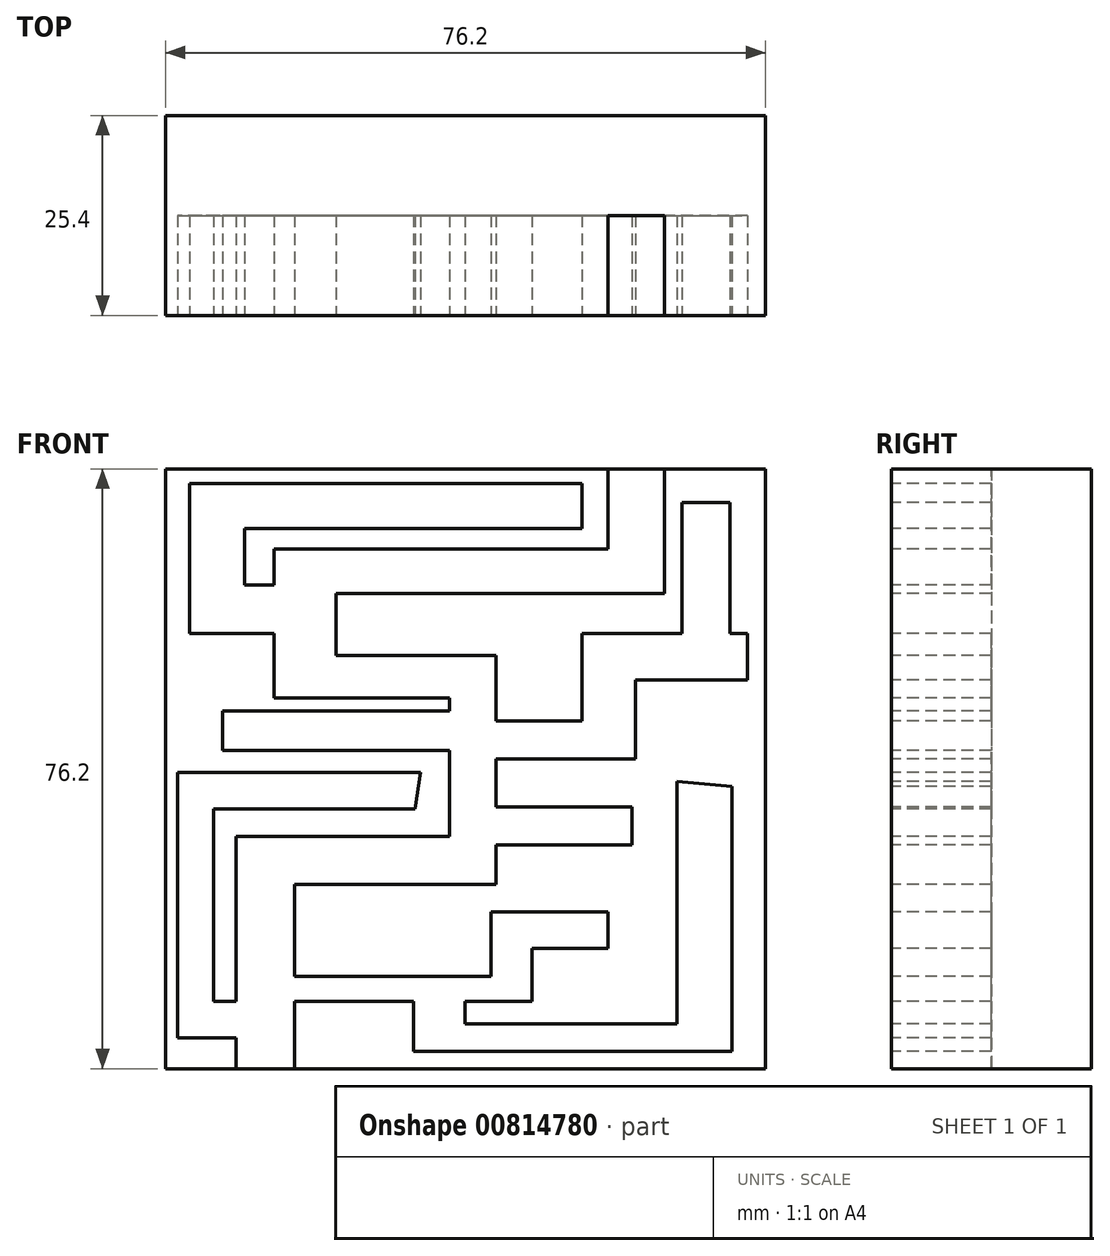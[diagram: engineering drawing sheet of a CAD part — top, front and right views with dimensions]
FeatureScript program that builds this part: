
annotation { "Feature Type Name" : "Feature", "Feature Type Description" : "" }
export const myFeature = defineFeature(function(context is Context, id is Id, definition is map)
    precondition{}
    {
        {
            var Q0;
            Q0=qCreatedBy(makeId("Front.planeOp"),FACE);
            var sketch = newSketch(context, id + "F0", { "sketchPlane" : qUnion([Q0])});
            skLineSegment(sketch, "E0.bottom", {"start": v(-38.04, 29.1) * mm, "end": v(38.16, 29.1) * mm});
            skLineSegment(sketch, "E0.top", {"start": v(-38.04, -47.1) * mm, "end": v(38.16, -47.1) * mm});
            skLineSegment(sketch, "E0.left", {"start": v(-38.04, 29.1) * mm, "end": v(-38.04, -47.1) * mm});
            skLineSegment(sketch, "E0.right", {"start": v(38.16, 29.1) * mm, "end": v(38.16, -47.1) * mm});
            skSolve(sketch);
        }
        {
            var Q0;
            Q0 = qSketchRegion(id + "F0", true);
            extrude(context, id + "F1", {"entities" : qUnion([Q0]), "depth" : 25.4 * mm, "offsetDistance" : 25.4 * mm});
        }
        {
            var Q0;
            Q0=makeQuery(id+"F1.opExtrude","CAP_FACE",FACE,{"disambiguationData":[OSD([sQuery(id+"F0.wireOp",EDGE,"E0.bottom"),sQuery(id+"F0.wireOp",EDGE,"E0.top"),sQuery(id+"F0.wireOp",EDGE,"E0.left"),sQuery(id+"F0.wireOp",EDGE,"E0.right")])],"isStart":false});
            var sketch = newSketch(context, id + "F2", { "sketchPlane" : qUnion([Q0])});
            skLineSegment(sketch, "E1", {"start": v(-29.07, -47.1) * mm, "end": v(-29.07, -43.17) * mm});
            skLineSegment(sketch, "E2", {"start": v(-29.07, -17.6) * mm, "end": v(-1.97, -17.6) * mm});
            skLineSegment(sketch, "E3", {"start": v(-1.97, -17.6) * mm, "end": v(-1.97, -6.67) * mm});
            skLineSegment(sketch, "E4", {"start": v(-1.97, 0) * mm, "end": v(-24.27, 0) * mm});
            skLineSegment(sketch, "E5", {"start": v(-24.27, 0) * mm, "end": v(-24.27, 8.2) * mm});
            skLineSegment(sketch, "E6", {"start": v(-24.27, 18.9) * mm, "end": v(18.14, 18.9) * mm});
            skLineSegment(sketch, "E7", {"start": v(18.14, 18.9) * mm, "end": v(18.14, 29.1) * mm});
            skLineSegment(sketch, "E8", {"start": v(25.36, 29.1) * mm, "end": v(25.36, 13.23) * mm});
            skLineSegment(sketch, "E9", {"start": v(25.36, 13.23) * mm, "end": v(-16.4, 13.23) * mm});
            skLineSegment(sketch, "E10", {"start": v(-16.4, 13.23) * mm, "end": v(-16.4, 5.36) * mm});
            skLineSegment(sketch, "E11", {"start": v(-16.4, 5.36) * mm, "end": v(3.93, 5.36) * mm});
            skLineSegment(sketch, "E12", {"start": v(3.93, 5.36) * mm, "end": v(3.93, -2.95) * mm});
            skLineSegment(sketch, "E13", {"start": v(3.93, -23.72) * mm, "end": v(-21.64, -23.72) * mm});
            skLineSegment(sketch, "E14", {"start": v(-21.64, -23.72) * mm, "end": v(-21.64, -35.41) * mm});
            skLineSegment(sketch, "E15", {"start": v(-21.64, -47.1) * mm, "end": v(-29.07, -47.1) * mm});
            skLineSegment(sketch, "E16", {"start": v(18.14, 29.1) * mm, "end": v(25.36, 29.1) * mm});
            skLineSegment(sketch, "E17", {"start": v(-21.64, -35.41) * mm, "end": v(3.28, -35.41) * mm});
            skLineSegment(sketch, "E18", {"start": v(3.28, -35.41) * mm, "end": v(3.28, -27.22) * mm});
            skLineSegment(sketch, "E19", {"start": v(3.28, -27.22) * mm, "end": v(18.14, -27.22) * mm});
            skLineSegment(sketch, "E20", {"start": v(18.14, -27.22) * mm, "end": v(18.14, -31.8) * mm});
            skLineSegment(sketch, "E21", {"start": v(18.14, -31.8) * mm, "end": v(8.53, -31.8) * mm});
            skLineSegment(sketch, "E22", {"start": v(8.53, -31.8) * mm, "end": v(8.53, -38.58) * mm});
            skLineSegment(sketch, "E23", {"start": v(8.53, -38.58) * mm, "end": v(0, -38.58) * mm});
            skLineSegment(sketch, "E24", {"start": v(-6.56, -38.58) * mm, "end": v(-6.56, -44.92) * mm});
            skLineSegment(sketch, "E25", {"start": v(-6.56, -44.92) * mm, "end": v(33.88, -44.92) * mm});
            skLineSegment(sketch, "E26", {"start": v(33.88, -44.92) * mm, "end": v(33.88, -11.26) * mm});
            skLineSegment(sketch, "E27", {"start": v(0, -38.58) * mm, "end": v(0, -41.43) * mm});
            skLineSegment(sketch, "E28", {"start": v(0, -41.43) * mm, "end": v(26.89, -41.43) * mm});
            skLineSegment(sketch, "E29", {"start": v(26.89, -41.43) * mm, "end": v(26.89, -10.6) * mm});
            skLineSegment(sketch, "E30", {"start": v(26.89, -10.6) * mm, "end": v(33.88, -11.26) * mm});
            skLineSegment(sketch, "E31.trimOffspring", {"start": v(-6.56, -38.58) * mm, "end": v(-21.64, -38.58) * mm});
            skLineSegment(sketch, "E32.trimOffspring", {"start": v(-21.64, -38.58) * mm, "end": v(-21.64, -47.1) * mm});
            skLineSegment(sketch, "E33", {"start": v(-29.07, -38.58) * mm, "end": v(-31.92, -38.58) * mm});
            skPoint(sketch, "E33.startSnap0", {"position": v(-14.1, -38.58) * mm});
            skLineSegment(sketch, "E34", {"start": v(-31.92, -38.58) * mm, "end": v(-31.92, -14.1) * mm});
            skLineSegment(sketch, "E35", {"start": v(-31.92, -14.1) * mm, "end": v(-6.34, -14.1) * mm});
            skLineSegment(sketch, "E36", {"start": v(-29.07, -43.17) * mm, "end": v(-36.5, -43.17) * mm});
            skLineSegment(sketch, "E37", {"start": v(-36.5, -43.17) * mm, "end": v(-36.5, -9.5) * mm});
            skLineSegment(sketch, "E38", {"start": v(-36.5, -9.5) * mm, "end": v(-5.68, -9.5) * mm});
            skLineSegment(sketch, "E39", {"start": v(-5.68, -9.5) * mm, "end": v(-6.34, -14.1) * mm});
            skLineSegment(sketch, "E40.trimOffspring", {"start": v(-29.07, -38.58) * mm, "end": v(-29.07, -17.6) * mm});
            skLineSegment(sketch, "E41", {"start": v(3.93, -2.95) * mm, "end": v(14.87, -2.95) * mm});
            skLineSegment(sketch, "E42", {"start": v(14.87, -2.95) * mm, "end": v(14.87, 8.2) * mm});
            skLineSegment(sketch, "E43", {"start": v(14.87, 8.2) * mm, "end": v(27.54, 8.2) * mm});
            skLineSegment(sketch, "E44", {"start": v(35.85, 8.2) * mm, "end": v(35.85, 2.3) * mm});
            skLineSegment(sketch, "E45", {"start": v(35.85, 2.3) * mm, "end": v(21.64, 2.3) * mm});
            skLineSegment(sketch, "E46", {"start": v(21.64, 2.3) * mm, "end": v(21.64, -7.76) * mm});
            skLineSegment(sketch, "E47", {"start": v(21.64, -7.76) * mm, "end": v(3.93, -7.76) * mm});
            skLineSegment(sketch, "E48", {"start": v(3.93, -13.88) * mm, "end": v(21.2, -13.88) * mm});
            skLineSegment(sketch, "E49", {"start": v(21.2, -13.88) * mm, "end": v(21.2, -18.7) * mm});
            skLineSegment(sketch, "E50", {"start": v(21.2, -18.7) * mm, "end": v(3.93, -18.7) * mm});
            skLineSegment(sketch, "E51.trimOffspring", {"start": v(3.93, -18.7) * mm, "end": v(3.93, -23.72) * mm});
            skLineSegment(sketch, "E52.trimOffspring", {"start": v(3.93, -7.76) * mm, "end": v(3.93, -13.88) * mm});
            skLineSegment(sketch, "E53", {"start": v(-24.27, 14.32) * mm, "end": v(-27.98, 14.32) * mm});
            skLineSegment(sketch, "E54", {"start": v(-27.98, 14.32) * mm, "end": v(-27.98, 21.53) * mm});
            skLineSegment(sketch, "E55", {"start": v(-27.98, 21.53) * mm, "end": v(14.87, 21.53) * mm});
            skLineSegment(sketch, "E56", {"start": v(14.87, 21.53) * mm, "end": v(14.87, 27.22) * mm});
            skLineSegment(sketch, "E57", {"start": v(14.87, 27.22) * mm, "end": v(-34.98, 27.22) * mm});
            skLineSegment(sketch, "E58", {"start": v(-34.98, 27.22) * mm, "end": v(-34.98, 8.2) * mm});
            skLineSegment(sketch, "E59", {"start": v(-34.98, 8.2) * mm, "end": v(-24.27, 8.2) * mm});
            skLineSegment(sketch, "E60", {"start": v(-1.97, -1.64) * mm, "end": v(-30.82, -1.64) * mm});
            skLineSegment(sketch, "E61", {"start": v(-30.82, -1.64) * mm, "end": v(-30.82, -6.67) * mm});
            skLineSegment(sketch, "E62", {"start": v(-30.82, -6.67) * mm, "end": v(-1.97, -6.67) * mm});
            skLineSegment(sketch, "E63", {"start": v(27.54, 8.2) * mm, "end": v(27.54, 24.81) * mm});
            skLineSegment(sketch, "E64", {"start": v(27.54, 24.81) * mm, "end": v(33.67, 24.81) * mm});
            skLineSegment(sketch, "E65", {"start": v(33.67, 24.81) * mm, "end": v(33.67, 8.2) * mm});
            skLineSegment(sketch, "E66.trimOffspring", {"start": v(33.67, 8.2) * mm, "end": v(35.85, 8.2) * mm});
            skLineSegment(sketch, "E67.trimOffspring", {"start": v(-24.27, 14.32) * mm, "end": v(-24.27, 18.9) * mm});
            skLineSegment(sketch, "E68.trimOffspring", {"start": v(-1.97, -1.64) * mm, "end": v(-1.97, 0) * mm});
            skArc(sketch, "E69", {"start": v(0, 55.2) * mm, "mid": v(1.85, 58.47) * mm, "end": v(0, 61.74) * mm});
            skLineSegment(sketch, "E70", {"start": v(0, 61.74) * mm, "end": v(0, 55.2) * mm});
            skSolve(sketch);
        }
        {
            var Q0;
            Q0 = qSketchRegion(id + "F2", true);
            extrude(context, id + "F3", {"entities" : qUnion([Q0]), "operationType" : NewBodyOperationType.REMOVE, "oppositeDirection" : true, "depth" : 12.7 * mm, "offsetDistance" : 25.4 * mm});
        }
    });
